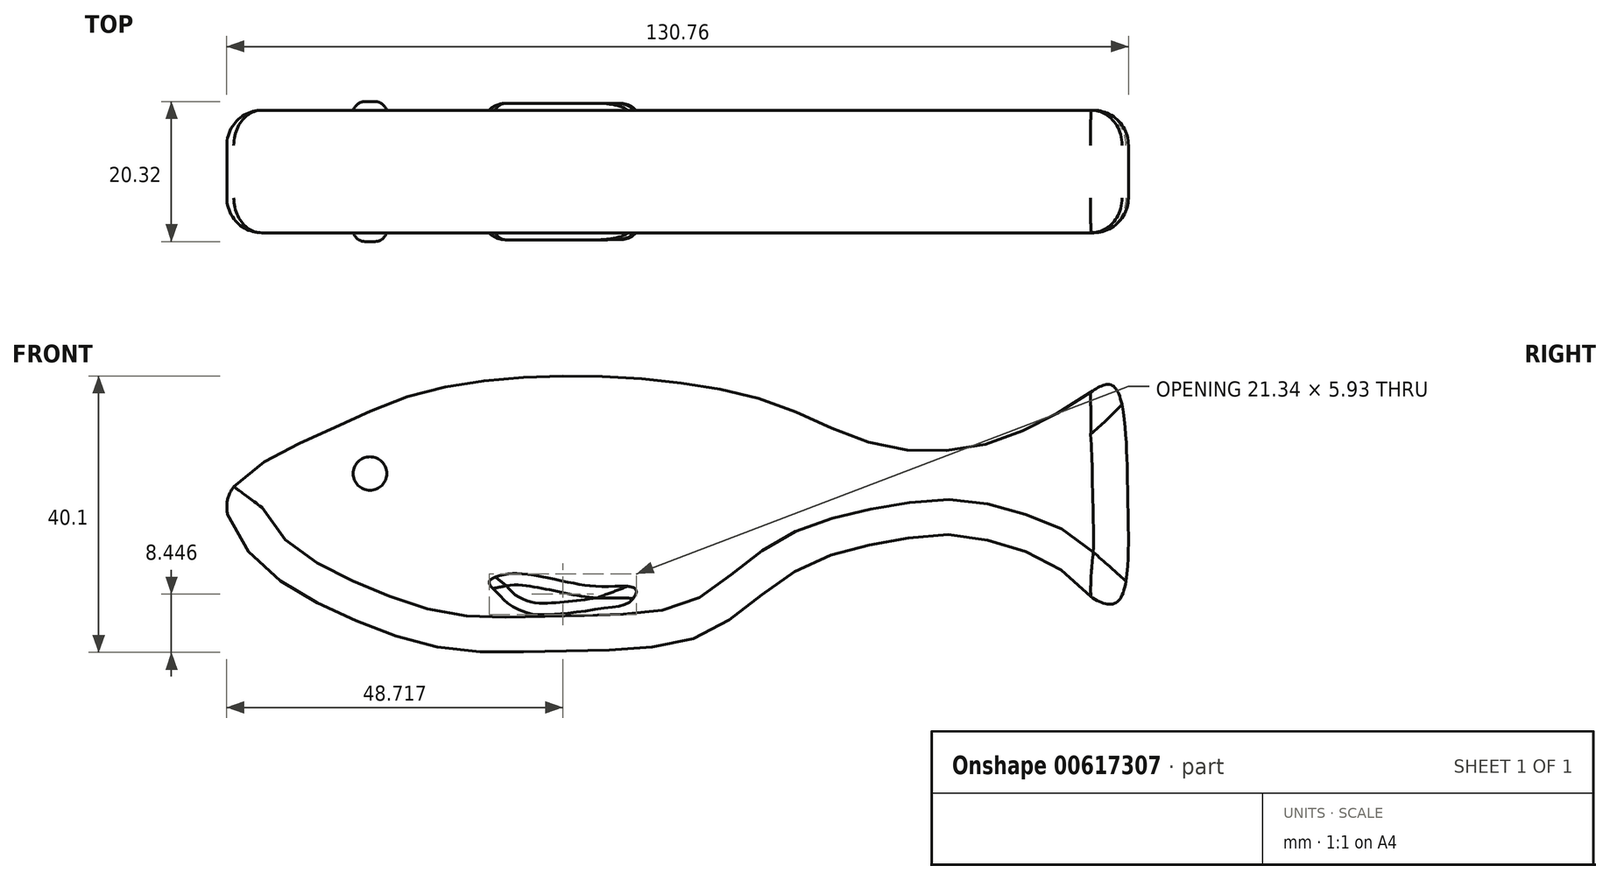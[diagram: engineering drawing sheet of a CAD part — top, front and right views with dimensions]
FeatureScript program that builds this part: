
annotation { "Feature Type Name" : "Feature", "Feature Type Description" : "" }
export const myFeature = defineFeature(function(context is Context, id is Id, definition is map)
    precondition{}
    {
        {
            var Q0;
            Q0=qCreatedBy(makeId("Front.planeOp"),FACE);
            var sketch = newSketch(context, id + "F0", { "sketchPlane" : qUnion([Q0])});
            skFitSpline(sketch, "E0", {"points": [v(-73, 0) * mm, v(-58.97, 9.52) * mm, v(-43.95, 15.53) * mm, v(-17.9, 17.53) * mm, v(5.13, 14.02) * mm, v(14.65, 10.02) * mm, v(24.67, 7.01) * mm, v(36.94, 7.76) * mm, v(45.95, 11.52) * mm, v(50.96, 14.52) * mm, v(55.22, 16.28) * mm, v(57.47, 0) * mm, v(55.72, -15.28) * mm, v(50.96, -13.52) * mm, v(47.2, -10.02) * mm, v(40.94, -7.26) * mm, v(33.68, -5.5) * mm, v(26.42, -5.76) * mm, v(16.4, -7.76) * mm, v(7.89, -11.52) * mm, v(-2.38, -19.03) * mm, v(-12.4, -21.79) * mm, v(-26.42, -22.29) * mm, v(-38.19, -22.29) * mm, v(-48.7, -20.03) * mm, v(-60.48, -15.03) * mm, v(-68.5, -9.52) * mm, v(-73, 0) * mm]});
            skSolve(sketch);
        }
        {
            var Q0;
            Q0=makeQuery(id+"F0.imprint","IMPRINT",FACE,{"disambiguationData":[TD([[makeQuery(id+"F0.imprint","IMPRINT",EDGE,{"derivedFrom":sQuery(id+"F0.wireOp",EDGE,"E0")}),-1.0]])]});
            extrude(context, id + "F1", {"entities" : qUnion([Q0]), "depth" : 8.9 * mm, "offsetDistance" : 25.4 * mm});
        }
        {
            var Q0;
            Q0=makeQuery(id+"F1.opExtrude","CAP_FACE",FACE,{"disambiguationData":[OSD([sQuery(id+"F0.wireOp",EDGE,"E0")])],"isStart":false});
            fillet(context, id + "F2", {"entities" : qUnion([Q0]), "radius" : 5.08 * mm, "tangentPropagation" : true, "allowEdgeOverflow" : false});
        }
        {
            var Q0;
            Q0=qCreatedBy(makeId("Front.planeOp"),FACE);
            var sketch = newSketch(context, id + "F3", { "sketchPlane" : qUnion([Q0])});
            skCircle(sketch, "E1", {"center": v(-52.42, 3.5) * mm, "radius": 2.43 * mm});
            skSolve(sketch);
        }
        {
            var Q0;
            Q0=makeQuery(id+"F3.imprint","IMPRINT",FACE,{"disambiguationData":[TD([[makeQuery(id+"F3.imprint","IMPRINT",EDGE,{"derivedFrom":sQuery(id+"F3.wireOp",EDGE,"E1")}),1.0]])]});
            extrude(context, id + "F4", {"entities" : qUnion([Q0]), "operationType" : NewBodyOperationType.ADD, "depth" : 10.16 * mm, "offsetDistance" : 25.4 * mm});
        }
        {
            var Q0;
            Q0=makeQuery(id+"F4.opExtrude","CAP_EDGE",EDGE,{"disambiguationData":[OSD([sQuery(id+"F3.wireOp",EDGE,"E1")])],"isStart":false});
            fillet(context, id + "F5", {"entities" : qUnion([Q0]), "radius" : 1.84 * mm, "tangentPropagation" : true, "allowEdgeOverflow" : false});
        }
        {
            var Q0;
            Q0=qCreatedBy(makeId("Front.planeOp"),FACE);
            var sketch = newSketch(context, id + "F6", { "sketchPlane" : qUnion([Q0])});
            skFitSpline(sketch, "E2", {"points": [v(-33.46, -11.29) * mm, v(-30.26, -11.06) * mm, v(-23.56, -12.3) * mm, v(-18.6, -12.9) * mm, v(-13.9, -13.31) * mm, v(-14.66, -15.06) * mm, v(-17.2, -15.87) * mm, v(-23.56, -16.74) * mm, v(-26.76, -16.96) * mm, v(-29.28, -16.82) * mm, v(-32.56, -15.25) * mm, v(-33.9, -13.86) * mm, v(-35.15, -12.25) * mm, v(-33.46, -11.29) * mm]});
            skSolve(sketch);
        }
        {
            var Q0;
            Q0=makeQuery(id+"F6.imprint","IMPRINT",FACE,{"disambiguationData":[TD([[makeQuery(id+"F6.imprint","IMPRINT",EDGE,{"derivedFrom":sQuery(id+"F6.wireOp",EDGE,"E2")}),-1.0]])]});
            extrude(context, id + "F7", {"entities" : qUnion([Q0]), "operationType" : NewBodyOperationType.ADD, "depth" : 9.9 * mm, "offsetDistance" : 25.4 * mm});
        }
        {
            var Q0;
            Q0=makeQuery(id+"F7.opExtrude","CAP_EDGE",EDGE,{"disambiguationData":[OSD([sQuery(id+"F6.wireOp",EDGE,"E2")])],"isStart":false});
            fillet(context, id + "F8", {"entities" : qUnion([Q0]), "radius" : 1.84 * mm, "tangentPropagation" : true, "allowEdgeOverflow" : false});
        }
        {
            var Q0;
            Q0=makeQuery(id+"F1.opExtrude","SWEPT_BODY",BODY,{"disambiguationData":[OSD([sQuery(id+"F0.wireOp",EDGE,"E0")])]});
            var Q1;
            Q1=qCreatedBy(makeId("Front.planeOp"),FACE);
            mirror(context, id + "F9", {"operationType" : NewBodyOperationType.ADD, "entities" : qUnion([Q0]), "mirrorPlane" : qUnion([Q1])});
        }
    });
